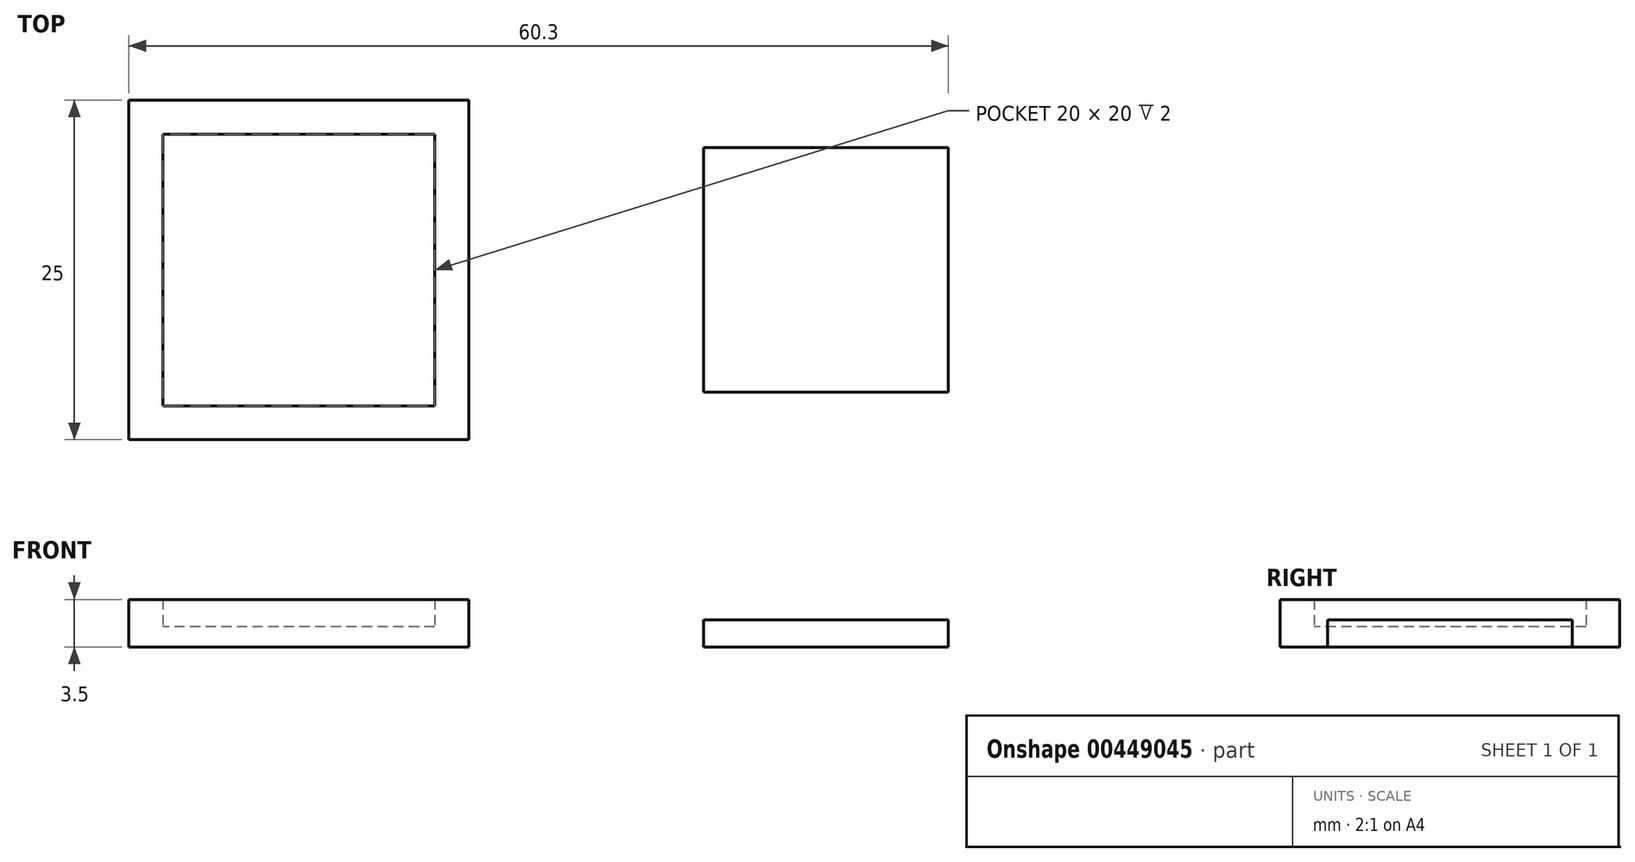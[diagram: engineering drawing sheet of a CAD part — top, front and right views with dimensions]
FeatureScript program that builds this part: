
annotation { "Feature Type Name" : "Feature", "Feature Type Description" : "" }
export const myFeature = defineFeature(function(context is Context, id is Id, definition is map)
    precondition{}
    {
        {
            var Q0;
            Q0=qCreatedBy(makeId("Top.planeOp"),FACE);
            var sketch = newSketch(context, id + "F0", { "sketchPlane" : qUnion([Q0])});
            skLineSegment(sketch, "E0.bottom", {"start": v(10, 10) * mm, "end": v(-10, 10) * mm});
            skLineSegment(sketch, "E0.top", {"start": v(10, -10) * mm, "end": v(-10, -10) * mm});
            skLineSegment(sketch, "E0.left", {"start": v(10, 10) * mm, "end": v(10, -10) * mm});
            skLineSegment(sketch, "E0.right", {"start": v(-10, 10) * mm, "end": v(-10, -10) * mm});
            skPoint(sketch, "E0.middle", {"position": v(0, 0) * mm});
            skLineSegment(sketch, "E1.bottom", {"start": v(12.5, 12.5) * mm, "end": v(-12.5, 12.5) * mm});
            skLineSegment(sketch, "E1.top", {"start": v(12.5, -12.5) * mm, "end": v(-12.5, -12.5) * mm});
            skLineSegment(sketch, "E1.left", {"start": v(12.5, 12.5) * mm, "end": v(12.5, -12.5) * mm});
            skLineSegment(sketch, "E1.right", {"start": v(-12.5, 12.5) * mm, "end": v(-12.5, -12.5) * mm});
            skLineSegment(sketch, "E2.bottom", {"start": v(9, 9) * mm, "end": v(-9, 9) * mm});
            skLineSegment(sketch, "E2.top", {"start": v(9, -9) * mm, "end": v(-9, -9) * mm});
            skLineSegment(sketch, "E2.left", {"start": v(9, 9) * mm, "end": v(9, -9) * mm});
            skLineSegment(sketch, "E2.right", {"start": v(-9, 9) * mm, "end": v(-9, -9) * mm});
            skLineSegment(sketch, "E3.bottom", {"start": v(29.8, 9) * mm, "end": v(47.8, 9) * mm});
            skLineSegment(sketch, "E3.top", {"start": v(29.8, -9) * mm, "end": v(47.8, -9) * mm});
            skLineSegment(sketch, "E3.left", {"start": v(29.8, 9) * mm, "end": v(29.8, -9) * mm});
            skLineSegment(sketch, "E3.right", {"start": v(47.8, 9) * mm, "end": v(47.8, -9) * mm});
            skPoint(sketch, "E3.middle", {"position": v(38.8, 0) * mm});
            skSolve(sketch);
        }
        {
            var Q0;
            Q0=makeQuery(id+"F0.imprint","IMPRINT",FACE,{"disambiguationData":[TD([[makeQuery(id+"F0.imprint","IMPRINT",EDGE,{"derivedFrom":sQuery(id+"F0.wireOp",EDGE,"E0.bottom")}),-1.0]])]});
            extrude(context, id + "F1", {"entities" : qUnion([Q0]), "depth" : 3.5 * mm});
        }
        {
            var Q0;
            Q0=makeQuery(id+"F0.imprint","IMPRINT",FACE,{"disambiguationData":[TD([[makeQuery(id+"F0.imprint","IMPRINT",EDGE,{"derivedFrom":sQuery(id+"F0.wireOp",EDGE,"E0.bottom")}),1.0]])]});
            var Q1;
            Q1=makeQuery(id+"F0.imprint","IMPRINT",FACE,{"disambiguationData":[TD([[makeQuery(id+"F0.imprint","IMPRINT",EDGE,{"derivedFrom":sQuery(id+"F0.wireOp",EDGE,"E2.bottom")}),1.0]])]});
            extrude(context, id + "F2", {"entities" : qUnion([Q0, Q1]), "operationType" : NewBodyOperationType.ADD, "depth" : 1.5 * mm});
        }
        {
            var Q0;
            Q0=makeQuery(id+"F0.imprint","IMPRINT",FACE,{"disambiguationData":[TD([[makeQuery(id+"F0.imprint","IMPRINT",EDGE,{"derivedFrom":sQuery(id+"F0.wireOp",EDGE,"E3.bottom")}),-1.0]])]});
            extrude(context, id + "F3", {"entities" : qUnion([Q0]), "depth" : 2 * mm});
        }
    });
